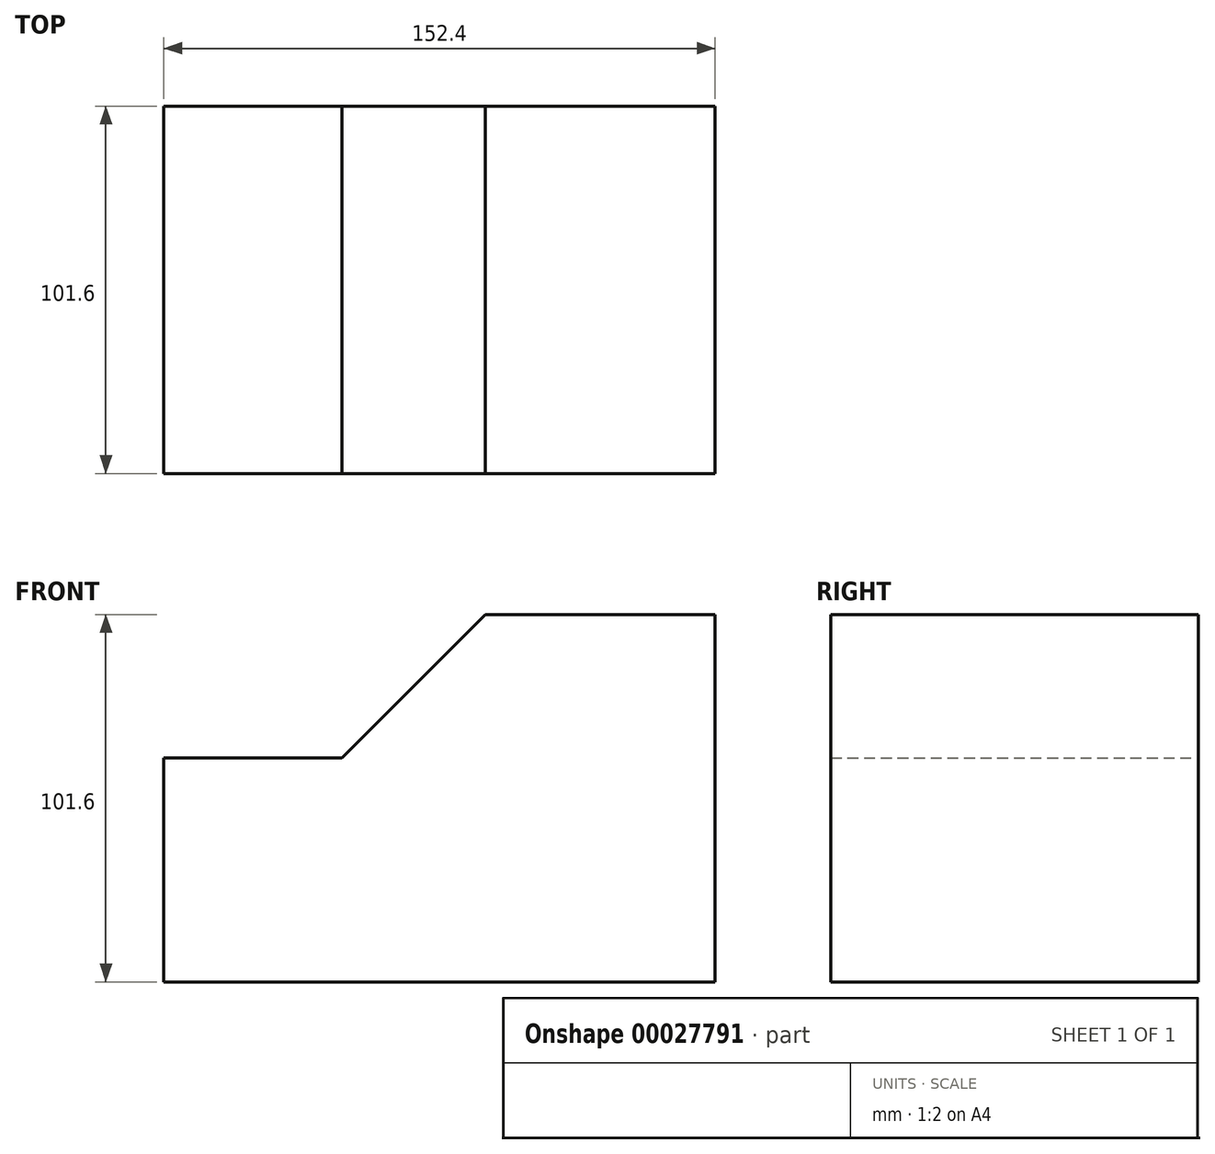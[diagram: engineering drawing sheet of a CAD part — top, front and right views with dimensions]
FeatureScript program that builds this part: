
annotation { "Feature Type Name" : "Feature", "Feature Type Description" : "" }
export const myFeature = defineFeature(function(context is Context, id is Id, definition is map)
    precondition{}
    {
        {
            var Q0;
            Q0=qCreatedBy(makeId("Front.planeOp"),FACE);
            var sketch = newSketch(context, id + "F0", { "sketchPlane" : qUnion([Q0])});
            skLineSegment(sketch, "E0", {"start": v(0, 0) * mm, "end": v(0, 61.91) * mm});
            skLineSegment(sketch, "E1", {"start": v(0, 61.91) * mm, "end": v(49.21, 61.91) * mm});
            skLineSegment(sketch, "E2", {"start": v(49.21, 61.91) * mm, "end": v(88.9, 101.6) * mm});
            skLineSegment(sketch, "E3", {"start": v(88.9, 101.6) * mm, "end": v(152.4, 101.6) * mm});
            skLineSegment(sketch, "E4", {"start": v(152.4, 101.6) * mm, "end": v(152.4, 0) * mm});
            skLineSegment(sketch, "E5", {"start": v(152.4, 0) * mm, "end": v(0, 0) * mm});
            skSolve(sketch);
        }
        {
            var Q0;
            Q0 = qSketchRegion(id + "F0", true);
            extrude(context, id + "F1", {"entities" : qUnion([Q0]), "endBound" : BoundingType.SYMMETRIC, "depth" : 101.6 * mm});
        }
    });
